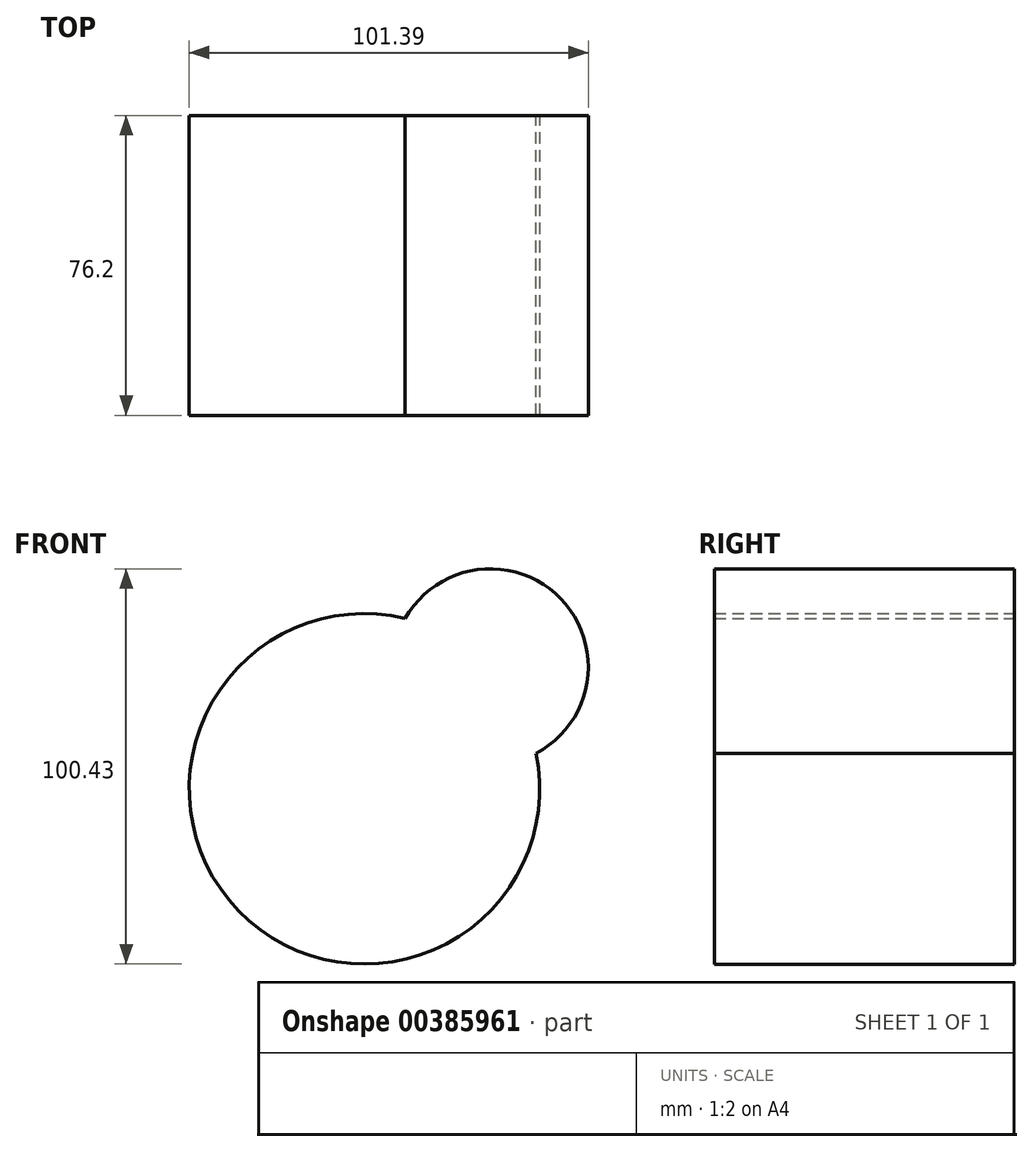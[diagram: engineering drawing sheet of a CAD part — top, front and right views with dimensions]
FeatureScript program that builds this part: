
annotation { "Feature Type Name" : "Feature", "Feature Type Description" : "" }
export const myFeature = defineFeature(function(context is Context, id is Id, definition is map)
    precondition{}
    {
        {
            var Q0;
            Q0=qCreatedBy(makeId("Front.planeOp"),FACE);
            var sketch = newSketch(context, id + "F0", { "sketchPlane" : qUnion([Q0])});
            skCircle(sketch, "E0", {"center": v(0, 0) * mm, "radius": 44.53 * mm});
            skCircle(sketch, "E1", {"center": v(31.96, 31) * mm, "radius": 24.9 * mm});
            skSolve(sketch);
        }
        {
            var Q0;
            Q0 = qSketchRegion(id + "F0", true);
            extrude(context, id + "F1", {"entities" : qUnion([Q0]), "depth" : 76.2 * mm});
        }
    });
